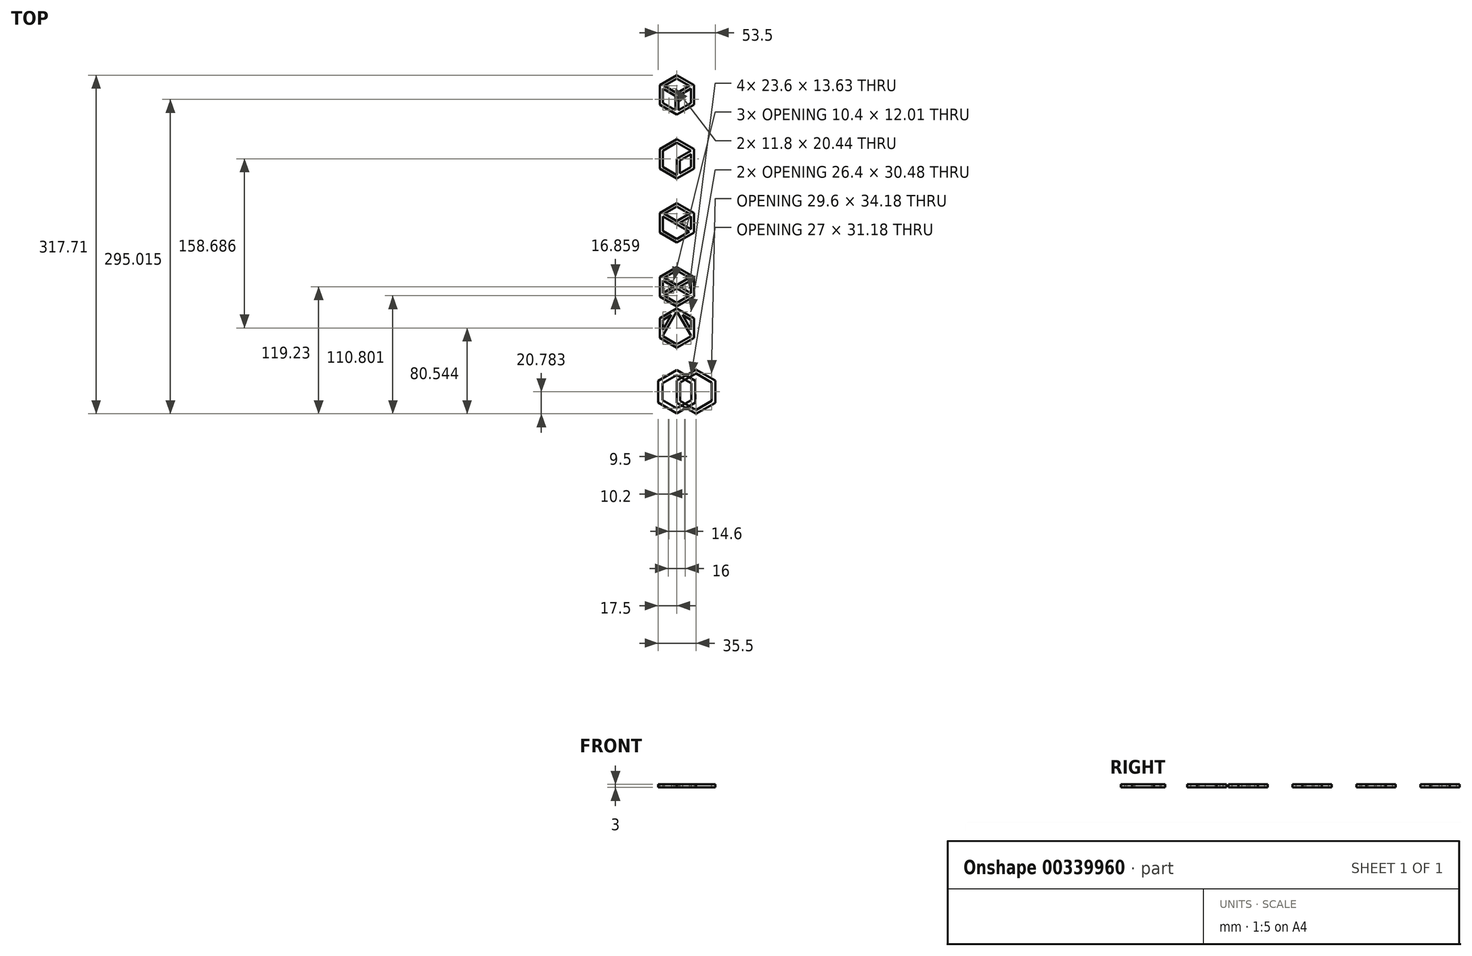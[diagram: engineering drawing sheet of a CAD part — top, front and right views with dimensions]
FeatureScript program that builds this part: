
annotation { "Feature Type Name" : "Feature", "Feature Type Description" : "" }
export const myFeature = defineFeature(function(context is Context, id is Id, definition is map)
    precondition{}
    {
        {
            var Q0;
            Q0=qCreatedBy(makeId("Top.planeOp"),FACE);
            var sketch = newSketch(context, id + "F0", { "sketchPlane" : qUnion([Q0])});
            skCircle(sketch, "E0.cCircle", {"center": v(0, 0) * mm, "radius": 16 * mm, "construction": true});
            skLineSegment(sketch, "E0.0", {"start": v(16, 9.24) * mm, "end": v(16, -9.24) * mm});
            skLineSegment(sketch, "E0.1", {"start": v(16, -9.24) * mm, "end": v(0, -18.48) * mm});
            skLineSegment(sketch, "E0.2", {"start": v(0, -18.48) * mm, "end": v(-16, -9.24) * mm});
            skLineSegment(sketch, "E0.3", {"start": v(-16, -9.24) * mm, "end": v(-16, 9.24) * mm});
            skLineSegment(sketch, "E0.4", {"start": v(-16, 9.24) * mm, "end": v(0, 18.48) * mm});
            skLineSegment(sketch, "E0.5", {"start": v(0, 18.48) * mm, "end": v(16, 9.24) * mm});
            skPoint(sketch, "E0.0.midPoint", {"position": v(16, 0) * mm});
            skLineSegment(sketch, "E1", {"start": v(16, 9.24) * mm, "end": v(0, 0) * mm});
            skLineSegment(sketch, "E2", {"start": v(0, -18.48) * mm, "end": v(0, 0) * mm});
            skLineSegment(sketch, "E3.0", {"start": v(-13.2, 7.62) * mm, "end": v(0, 15.24) * mm});
            skLineSegment(sketch, "E3.1", {"start": v(13.2, 7.62) * mm, "end": v(13.2, -7.62) * mm});
            skLineSegment(sketch, "E3.2", {"start": v(13.2, -7.62) * mm, "end": v(0, -15.24) * mm});
            skLineSegment(sketch, "E3.3", {"start": v(0, 15.24) * mm, "end": v(13.2, 7.62) * mm});
            skLineSegment(sketch, "E3.4", {"start": v(0, -15.24) * mm, "end": v(-13.2, -7.62) * mm});
            skLineSegment(sketch, "E3.5", {"start": v(-13.2, -7.62) * mm, "end": v(-13.2, 7.62) * mm});
            skLineSegment(sketch, "E4.0", {"start": v(2.8, -23.1) * mm, "end": v(2.8, -1.62) * mm});
            skLineSegment(sketch, "E4.1", {"start": v(21.4, 9.12) * mm, "end": v(2.8, -1.62) * mm});
            skSolve(sketch);
        }
        {
            var Q0;
            Q0 = qSketchRegion(id + "F0", true);
            var Q1;
            {var subQ3=sQuery(id+"F0.wireOp",EDGE,"E4.1");var subQ8=sQuery(id+"F0.wireOp",EDGE,"E4.0");var subQ11=makeQuery(id+"F0.imprint","INTERSECT",VERTEX,{"derivedFrom":[subQ8,subQ3]});Q1=makeQuery(id+"F0.imprint","IMPRINT",FACE,{"disambiguationData":[TD([[makeQuery(id+"F0.imprint","IMPRINT",EDGE,{"disambiguationData":[TD([[subQ11,1.0]])],"derivedFrom":subQ8}),1.0]])]});}
            extrude(context, id + "F1", {"entities" : qUnion([Q0, Q1]), "depth" : 3 * mm});
        }
        {
            var Q0;
            Q0=qCreatedBy(makeId("Top.planeOp"),FACE);
            var sketch = newSketch(context, id + "F2", { "sketchPlane" : qUnion([Q0])});
            skCircle(sketch, "E5.cCircle", {"center": v(0, -60) * mm, "radius": 16 * mm, "construction": true});
            skLineSegment(sketch, "E5.0", {"start": v(16, -50.76) * mm, "end": v(16, -69.24) * mm});
            skLineSegment(sketch, "E5.1", {"start": v(16, -69.24) * mm, "end": v(0, -78.48) * mm});
            skLineSegment(sketch, "E5.2", {"start": v(0, -78.48) * mm, "end": v(-16, -69.24) * mm});
            skLineSegment(sketch, "E5.3", {"start": v(-16, -69.24) * mm, "end": v(-16, -50.76) * mm});
            skLineSegment(sketch, "E5.4", {"start": v(-16, -50.76) * mm, "end": v(0, -41.52) * mm});
            skLineSegment(sketch, "E5.5", {"start": v(0, -41.52) * mm, "end": v(16, -50.76) * mm});
            skPoint(sketch, "E5.0.midPoint", {"position": v(16, -60) * mm});
            skLineSegment(sketch, "E6.0", {"start": v(-13.2, -67.62) * mm, "end": v(-13.2, -52.38) * mm});
            skLineSegment(sketch, "E6.1", {"start": v(0, -44.76) * mm, "end": v(13.2, -52.38) * mm});
            skLineSegment(sketch, "E6.2", {"start": v(13.2, -52.38) * mm, "end": v(13.2, -67.62) * mm});
            skLineSegment(sketch, "E6.3", {"start": v(-13.2, -52.38) * mm, "end": v(0, -44.76) * mm});
            skLineSegment(sketch, "E6.4", {"start": v(13.2, -67.62) * mm, "end": v(0, -75.24) * mm});
            skLineSegment(sketch, "E6.5", {"start": v(0, -75.24) * mm, "end": v(-13.2, -67.62) * mm});
            skLineSegment(sketch, "E7", {"start": v(-16, -50.76) * mm, "end": v(16, -69.24) * mm});
            skLineSegment(sketch, "E8", {"start": v(0, -60) * mm, "end": v(16, -50.76) * mm});
            skLineSegment(sketch, "E9.0", {"start": v(-20.7, -49.67) * mm, "end": v(19.3, -72.76) * mm});
            skLineSegment(sketch, "E10.0", {"start": v(-19.3, -47.24) * mm, "end": v(20.7, -70.33) * mm});
            skLineSegment(sketch, "E11.0", {"start": v(-3.3, -63.52) * mm, "end": v(16.7, -51.97) * mm});
            skLineSegment(sketch, "E12.0", {"start": v(-4.7, -61.1) * mm, "end": v(15.3, -49.55) * mm});
            skSolve(sketch);
        }
        {
            var Q0;
            Q0 = qSketchRegion(id + "F2", true);
            var Q1;
            {var subQ4=sQuery(id+"F2.wireOp",EDGE,"E7");var subQ6=sQuery(id+"F2.wireOp",EDGE,"E8");var subQ7=makeQuery(id+"F2.imprint","INTERSECT",VERTEX,{"derivedFrom":[subQ4,subQ6]});Q1=makeQuery(id+"F2.imprint","IMPRINT",FACE,{"disambiguationData":[TD([[makeQuery(id+"F2.imprint","IMPRINT",EDGE,{"disambiguationData":[TD([[subQ7,-1.0]])],"derivedFrom":subQ6}),1.0]])]});}
            var Q2;
            {var subQ0=sQuery(id+"F2.wireOp",EDGE,"E7");var subQ3=makeQuery(id+"F2.imprint","INTERSECT",VERTEX,{"derivedFrom":[subQ0,sQuery(id+"F2.wireOp",EDGE,"E8")]});Q2=makeQuery(id+"F2.imprint","IMPRINT",FACE,{"disambiguationData":[TD([[makeQuery(id+"F2.imprint","IMPRINT",EDGE,{"disambiguationData":[TD([[subQ3,-1.0]])],"derivedFrom":subQ0}),-1.0]])]});}
            var Q3;
            {var subQ1=sQuery(id+"F2.wireOp",EDGE,"E6.2");var subQ3=sQuery(id+"F2.wireOp",EDGE,"E10.0");var subQ4=makeQuery(id+"F2.imprint","INTERSECT",VERTEX,{"derivedFrom":[subQ1,subQ3]});Q3=makeQuery(id+"F2.imprint","IMPRINT",FACE,{"disambiguationData":[TD([[makeQuery(id+"F2.imprint","IMPRINT",EDGE,{"disambiguationData":[TD([[subQ4,1.0]])],"derivedFrom":subQ3}),-1.0]])]});}
            var Q4;
            {var subQ0=sQuery(id+"F2.wireOp",EDGE,"E8");var subQ1=sQuery(id+"F2.wireOp",EDGE,"E7");var subQ2=makeQuery(id+"F2.imprint","INTERSECT",VERTEX,{"derivedFrom":[subQ1,subQ0]});Q4=makeQuery(id+"F2.imprint","IMPRINT",FACE,{"disambiguationData":[TD([[makeQuery(id+"F2.imprint","IMPRINT",EDGE,{"disambiguationData":[TD([[subQ2,-1.0]])],"derivedFrom":subQ1}),1.0]])]});}
            var Q5;
            {var subQ0=sQuery(id+"F2.wireOp",EDGE,"E8");var subQ5=sQuery(id+"F2.wireOp",EDGE,"E10.0");var subQ6=makeQuery(id+"F2.imprint","INTERSECT",VERTEX,{"derivedFrom":[subQ0,subQ5]});Q5=makeQuery(id+"F2.imprint","IMPRINT",FACE,{"disambiguationData":[TD([[makeQuery(id+"F2.imprint","IMPRINT",EDGE,{"disambiguationData":[TD([[subQ6,-1.0]])],"derivedFrom":subQ5}),1.0]])]});}
            var Q6;
            {var subQ3=sQuery(id+"F2.wireOp",EDGE,"E12.0");var subQ5=sQuery(id+"F2.wireOp",EDGE,"E10.0");var subQ7=makeQuery(id+"F2.imprint","INTERSECT",VERTEX,{"derivedFrom":[subQ5,subQ3]});Q6=makeQuery(id+"F2.imprint","IMPRINT",FACE,{"disambiguationData":[TD([[makeQuery(id+"F2.imprint","IMPRINT",EDGE,{"disambiguationData":[TD([[subQ7,-1.0]])],"derivedFrom":subQ5}),1.0]])]});}
            var Q7;
            {var subQ3=sQuery(id+"F2.wireOp",EDGE,"E9.0");var subQ5=sQuery(id+"F2.wireOp",EDGE,"E11.0");var subQ6=makeQuery(id+"F2.imprint","INTERSECT",VERTEX,{"derivedFrom":[subQ3,subQ5]});Q7=makeQuery(id+"F2.imprint","IMPRINT",FACE,{"disambiguationData":[TD([[makeQuery(id+"F2.imprint","IMPRINT",EDGE,{"disambiguationData":[TD([[subQ6,-1.0]])],"derivedFrom":subQ3}),1.0]])]});}
            var Q8;
            {var subQ3=sQuery(id+"F2.wireOp",EDGE,"E9.0");var subQ5=sQuery(id+"F2.wireOp",EDGE,"E12.0");var subQ6=makeQuery(id+"F2.imprint","INTERSECT",VERTEX,{"derivedFrom":[subQ3,subQ5]});Q8=makeQuery(id+"F2.imprint","IMPRINT",FACE,{"disambiguationData":[TD([[makeQuery(id+"F2.imprint","IMPRINT",EDGE,{"disambiguationData":[TD([[subQ6,1.0]])],"derivedFrom":subQ3}),1.0]])]});}
            var Q9;
            {var subQ1=sQuery(id+"F2.wireOp",EDGE,"E6.3");var subQ3=sQuery(id+"F2.wireOp",EDGE,"E10.0");var subQ4=makeQuery(id+"F2.imprint","INTERSECT",VERTEX,{"derivedFrom":[subQ1,subQ3]});Q9=makeQuery(id+"F2.imprint","IMPRINT",FACE,{"disambiguationData":[TD([[makeQuery(id+"F2.imprint","IMPRINT",EDGE,{"disambiguationData":[TD([[subQ4,-1.0]])],"derivedFrom":subQ3}),-1.0]])]});}
            extrude(context, id + "F3", {"entities" : qUnion([Q0, Q1, Q2, Q3, Q4, Q5, Q6, Q7, Q8, Q9]), "depth" : 3 * mm});
        }
        {
            var Q0;
            Q0=qCreatedBy(makeId("Top.planeOp"),FACE);
            var sketch = newSketch(context, id + "F4", { "sketchPlane" : qUnion([Q0])});
            skCircle(sketch, "E13.cCircle", {"center": v(0, 60) * mm, "radius": 16 * mm, "construction": true});
            skLineSegment(sketch, "E13.0", {"start": v(16, 69.24) * mm, "end": v(16, 50.76) * mm});
            skLineSegment(sketch, "E13.1", {"start": v(16, 50.76) * mm, "end": v(0, 41.52) * mm});
            skLineSegment(sketch, "E13.2", {"start": v(0, 41.52) * mm, "end": v(-16, 50.76) * mm});
            skLineSegment(sketch, "E13.3", {"start": v(-16, 50.76) * mm, "end": v(-16, 69.24) * mm});
            skLineSegment(sketch, "E13.4", {"start": v(-16, 69.24) * mm, "end": v(0, 78.48) * mm});
            skLineSegment(sketch, "E13.5", {"start": v(0, 78.48) * mm, "end": v(16, 69.24) * mm});
            skPoint(sketch, "E13.0.midPoint", {"position": v(16, 60) * mm});
            skLineSegment(sketch, "E14.0", {"start": v(-13.2, 67.62) * mm, "end": v(0, 75.24) * mm});
            skLineSegment(sketch, "E14.1", {"start": v(13.2, 67.62) * mm, "end": v(13.2, 52.38) * mm});
            skLineSegment(sketch, "E14.2", {"start": v(13.2, 52.38) * mm, "end": v(0, 44.76) * mm});
            skLineSegment(sketch, "E14.3", {"start": v(0, 75.24) * mm, "end": v(13.2, 67.62) * mm});
            skLineSegment(sketch, "E14.4", {"start": v(0, 44.76) * mm, "end": v(-13.2, 52.38) * mm});
            skLineSegment(sketch, "E14.5", {"start": v(-13.2, 52.38) * mm, "end": v(-13.2, 67.62) * mm});
            skLineSegment(sketch, "E15", {"start": v(0, 41.52) * mm, "end": v(0, 60) * mm});
            skLineSegment(sketch, "E16", {"start": v(0, 60) * mm, "end": v(-16, 69.24) * mm});
            skLineSegment(sketch, "E17", {"start": v(0, 60) * mm, "end": v(16, 69.24) * mm});
            skLineSegment(sketch, "E18.0", {"start": v(0, 61.62) * mm, "end": v(-19.3, 72.76) * mm});
            skLineSegment(sketch, "E18.1", {"start": v(0, 61.62) * mm, "end": v(19.3, 72.76) * mm});
            skLineSegment(sketch, "E19.0", {"start": v(0, 58.38) * mm, "end": v(-20.7, 70.33) * mm});
            skLineSegment(sketch, "E19.1", {"start": v(0, 58.38) * mm, "end": v(20.7, 70.33) * mm});
            skLineSegment(sketch, "E20.0", {"start": v(1.4, 36.9) * mm, "end": v(1.4, 60) * mm});
            skLineSegment(sketch, "E21.0", {"start": v(-1.4, 36.9) * mm, "end": v(-1.4, 60) * mm});
            skSolve(sketch);
        }
        {
            var Q0;
            {var subQ7=sQuery(id+"F4.wireOp",EDGE,"E13.5");var subQ8=sQuery(id+"F4.wireOp",EDGE,"E13.4");var subQ9=makeQuery(id+"F4.imprint","INTERSECT",VERTEX,{"derivedFrom":[subQ8,subQ7]});Q0=makeQuery(id+"F4.imprint","IMPRINT",FACE,{"disambiguationData":[TD([[makeQuery(id+"F4.imprint","IMPRINT",EDGE,{"disambiguationData":[TD([[subQ9,1.0]])],"derivedFrom":subQ8}),-1.0]])]});}
            var Q1;
            {var subQ1=sQuery(id+"F4.wireOp",EDGE,"E13.4");var subQ3=sQuery(id+"F4.wireOp",EDGE,"E18.0");var subQ4=makeQuery(id+"F4.imprint","INTERSECT",VERTEX,{"derivedFrom":[subQ1,subQ3]});Q1=makeQuery(id+"F4.imprint","IMPRINT",FACE,{"disambiguationData":[TD([[makeQuery(id+"F4.imprint","IMPRINT",EDGE,{"disambiguationData":[TD([[subQ4,1.0]])],"derivedFrom":subQ3}),1.0]])]});}
            var Q2;
            {var subQ1=sQuery(id+"F4.wireOp",EDGE,"E13.3");var subQ3=sQuery(id+"F4.wireOp",EDGE,"E19.0");var subQ4=makeQuery(id+"F4.imprint","INTERSECT",VERTEX,{"derivedFrom":[subQ1,subQ3]});Q2=makeQuery(id+"F4.imprint","IMPRINT",FACE,{"disambiguationData":[TD([[makeQuery(id+"F4.imprint","IMPRINT",EDGE,{"disambiguationData":[TD([[subQ4,1.0]])],"derivedFrom":subQ3}),-1.0]])]});}
            var Q3;
            {var subQ0=sQuery(id+"F4.wireOp",EDGE,"E19.0");var subQ3=makeQuery(id+"F4.imprint","INTERSECT",VERTEX,{"derivedFrom":[subQ0,sQuery(id+"F4.wireOp",EDGE,"E21.0")]});Q3=makeQuery(id+"F4.imprint","IMPRINT",FACE,{"disambiguationData":[TD([[makeQuery(id+"F4.imprint","IMPRINT",EDGE,{"disambiguationData":[TD([[subQ3,-1.0]])],"derivedFrom":subQ0}),-1.0]])]});}
            var Q4;
            {var subQ5=sQuery(id+"F4.wireOp",EDGE,"E18.1");var subQ9=sQuery(id+"F4.wireOp",EDGE,"E18.0");var subQ11=makeQuery(id+"F4.imprint","INTERSECT",VERTEX,{"derivedFrom":[subQ9,subQ5]});Q4=makeQuery(id+"F4.imprint","IMPRINT",FACE,{"disambiguationData":[TD([[makeQuery(id+"F4.imprint","IMPRINT",EDGE,{"disambiguationData":[TD([[subQ11,-1.0]])],"derivedFrom":subQ9}),1.0]])]});}
            var Q5;
            {var subQ7=sQuery(id+"F4.wireOp",EDGE,"E13.2");var subQ9=sQuery(id+"F4.wireOp",EDGE,"E13.3");var subQ10=makeQuery(id+"F4.imprint","INTERSECT",VERTEX,{"derivedFrom":[subQ7,subQ9]});Q5=makeQuery(id+"F4.imprint","IMPRINT",FACE,{"disambiguationData":[TD([[makeQuery(id+"F4.imprint","IMPRINT",EDGE,{"disambiguationData":[TD([[subQ10,1.0]])],"derivedFrom":subQ7}),-1.0]])]});}
            var Q6;
            {var subQ3=sQuery(id+"F4.wireOp",EDGE,"E21.0");var subQ5=sQuery(id+"F4.wireOp",EDGE,"E19.0");var subQ7=makeQuery(id+"F4.imprint","INTERSECT",VERTEX,{"derivedFrom":[subQ5,subQ3]});Q6=makeQuery(id+"F4.imprint","IMPRINT",FACE,{"disambiguationData":[TD([[makeQuery(id+"F4.imprint","IMPRINT",EDGE,{"disambiguationData":[TD([[subQ7,1.0]])],"derivedFrom":subQ3}),-1.0]])]});}
            var Q7;
            {var subQ3=sQuery(id+"F4.wireOp",EDGE,"E20.0");var subQ5=sQuery(id+"F4.wireOp",EDGE,"E19.1");var subQ6=makeQuery(id+"F4.imprint","INTERSECT",VERTEX,{"derivedFrom":[subQ5,subQ3]});Q7=makeQuery(id+"F4.imprint","IMPRINT",FACE,{"disambiguationData":[TD([[makeQuery(id+"F4.imprint","IMPRINT",EDGE,{"disambiguationData":[TD([[subQ6,1.0]])],"derivedFrom":subQ3}),1.0]])]});}
            var Q8;
            {var subQ1=sQuery(id+"F4.wireOp",EDGE,"E13.2");var subQ3=sQuery(id+"F4.wireOp",EDGE,"E21.0");var subQ4=makeQuery(id+"F4.imprint","INTERSECT",VERTEX,{"derivedFrom":[subQ1,subQ3]});Q8=makeQuery(id+"F4.imprint","IMPRINT",FACE,{"disambiguationData":[TD([[makeQuery(id+"F4.imprint","IMPRINT",EDGE,{"disambiguationData":[TD([[subQ4,-1.0]])],"derivedFrom":subQ3}),-1.0]])]});}
            var Q9;
            {var subQ1=sQuery(id+"F4.wireOp",EDGE,"E13.1");var subQ3=sQuery(id+"F4.wireOp",EDGE,"E20.0");var subQ4=makeQuery(id+"F4.imprint","INTERSECT",VERTEX,{"derivedFrom":[subQ1,subQ3]});Q9=makeQuery(id+"F4.imprint","IMPRINT",FACE,{"disambiguationData":[TD([[makeQuery(id+"F4.imprint","IMPRINT",EDGE,{"disambiguationData":[TD([[subQ4,-1.0]])],"derivedFrom":subQ3}),1.0]])]});}
            var Q10;
            {var subQ5=sQuery(id+"F4.wireOp",EDGE,"E13.1");var subQ6=sQuery(id+"F4.wireOp",EDGE,"E13.0");var subQ7=makeQuery(id+"F4.imprint","INTERSECT",VERTEX,{"derivedFrom":[subQ6,subQ5]});Q10=makeQuery(id+"F4.imprint","IMPRINT",FACE,{"disambiguationData":[TD([[makeQuery(id+"F4.imprint","IMPRINT",EDGE,{"disambiguationData":[TD([[subQ7,1.0]])],"derivedFrom":subQ6}),-1.0]])]});}
            var Q11;
            {var subQ0=sQuery(id+"F4.wireOp",EDGE,"E19.1");var subQ3=makeQuery(id+"F4.imprint","INTERSECT",VERTEX,{"derivedFrom":[subQ0,sQuery(id+"F4.wireOp",EDGE,"E20.0")]});Q11=makeQuery(id+"F4.imprint","IMPRINT",FACE,{"disambiguationData":[TD([[makeQuery(id+"F4.imprint","IMPRINT",EDGE,{"disambiguationData":[TD([[subQ3,-1.0]])],"derivedFrom":subQ0}),1.0]])]});}
            var Q12;
            {var subQ1=sQuery(id+"F4.wireOp",EDGE,"E13.0");var subQ3=sQuery(id+"F4.wireOp",EDGE,"E19.1");var subQ4=makeQuery(id+"F4.imprint","INTERSECT",VERTEX,{"derivedFrom":[subQ1,subQ3]});Q12=makeQuery(id+"F4.imprint","IMPRINT",FACE,{"disambiguationData":[TD([[makeQuery(id+"F4.imprint","IMPRINT",EDGE,{"disambiguationData":[TD([[subQ4,1.0]])],"derivedFrom":subQ3}),1.0]])]});}
            var Q13;
            {var subQ1=sQuery(id+"F4.wireOp",EDGE,"E13.5");var subQ3=sQuery(id+"F4.wireOp",EDGE,"E18.1");var subQ4=makeQuery(id+"F4.imprint","INTERSECT",VERTEX,{"derivedFrom":[subQ1,subQ3]});Q13=makeQuery(id+"F4.imprint","IMPRINT",FACE,{"disambiguationData":[TD([[makeQuery(id+"F4.imprint","IMPRINT",EDGE,{"disambiguationData":[TD([[subQ4,1.0]])],"derivedFrom":subQ3}),-1.0]])]});}
            extrude(context, id + "F5", {"entities" : qUnion([Q0, Q1, Q2, Q3, Q4, Q5, Q6, Q7, Q8, Q9, Q10, Q11, Q12, Q13]), "depth" : 3 * mm});
        }
        {
            var Q0;
            Q0=qCreatedBy(makeId("Top.planeOp"),FACE);
            var sketch = newSketch(context, id + "F6", { "sketchPlane" : qUnion([Q0])});
            skCircle(sketch, "E22.cCircle", {"center": v(0, -120) * mm, "radius": 16 * mm, "construction": true});
            skLineSegment(sketch, "E22.0", {"start": v(16, -110.76) * mm, "end": v(16, -129.24) * mm});
            skLineSegment(sketch, "E22.1", {"start": v(16, -129.24) * mm, "end": v(0, -138.48) * mm});
            skLineSegment(sketch, "E22.2", {"start": v(0, -138.48) * mm, "end": v(-16, -129.24) * mm});
            skLineSegment(sketch, "E22.3", {"start": v(-16, -129.24) * mm, "end": v(-16, -110.76) * mm});
            skLineSegment(sketch, "E22.4", {"start": v(-16, -110.76) * mm, "end": v(0, -101.52) * mm});
            skLineSegment(sketch, "E22.5", {"start": v(0, -101.52) * mm, "end": v(16, -110.76) * mm});
            skPoint(sketch, "E22.0.midPoint", {"position": v(16, -120) * mm});
            skLineSegment(sketch, "E23", {"start": v(-16, -110.76) * mm, "end": v(16, -129.24) * mm});
            skLineSegment(sketch, "E24", {"start": v(-16, -129.24) * mm, "end": v(16, -110.76) * mm});
            skLineSegment(sketch, "E25.0", {"start": v(-13.2, -127.62) * mm, "end": v(-13.2, -112.38) * mm});
            skLineSegment(sketch, "E25.1", {"start": v(0, -104.76) * mm, "end": v(13.2, -112.38) * mm});
            skLineSegment(sketch, "E25.2", {"start": v(13.2, -112.38) * mm, "end": v(13.2, -127.62) * mm});
            skLineSegment(sketch, "E25.3", {"start": v(-13.2, -112.38) * mm, "end": v(0, -104.76) * mm});
            skLineSegment(sketch, "E25.4", {"start": v(13.2, -127.62) * mm, "end": v(0, -135.24) * mm});
            skLineSegment(sketch, "E25.5", {"start": v(0, -135.24) * mm, "end": v(-13.2, -127.62) * mm});
            skArc(sketch, "E26.0.startCap", {"start": v(-16.7, -111.97) * mm, "mid": v(-17.21, -110.06) * mm, "end": v(-15.3, -109.55) * mm});
            skArc(sketch, "E26.0.endCap", {"start": v(16.7, -128.03) * mm, "mid": v(17.21, -129.94) * mm, "end": v(15.3, -130.45) * mm});
            skLineSegment(sketch, "E26.0.left", {"start": v(-15.3, -109.55) * mm, "end": v(16.7, -128.03) * mm});
            skLineSegment(sketch, "E26.0.right", {"start": v(-16.7, -111.97) * mm, "end": v(15.3, -130.45) * mm});
            skArc(sketch, "E27.0.startCap", {"start": v(-15.3, -130.45) * mm, "mid": v(-17.21, -129.94) * mm, "end": v(-16.7, -128.03) * mm});
            skArc(sketch, "E27.0.endCap", {"start": v(15.3, -109.55) * mm, "mid": v(17.21, -110.06) * mm, "end": v(16.7, -111.97) * mm});
            skLineSegment(sketch, "E27.0.left", {"start": v(-16.7, -128.03) * mm, "end": v(15.3, -109.55) * mm});
            skLineSegment(sketch, "E27.0.right", {"start": v(-15.3, -130.45) * mm, "end": v(16.7, -111.97) * mm});
            skSolve(sketch);
        }
        {
            var Q0;
            {var subQ0=sQuery(id+"F6.wireOp",EDGE,"E27.0.right");var subQ1=sQuery(id+"F6.wireOp",EDGE,"E22.0");var subQ2=makeQuery(id+"F6.imprint","INTERSECT",VERTEX,{"derivedFrom":[subQ1,subQ0]});Q0=makeQuery(id+"F6.imprint","IMPRINT",FACE,{"disambiguationData":[TD([[makeQuery(id+"F6.imprint","IMPRINT",EDGE,{"disambiguationData":[TD([[subQ2,-1.0]])],"derivedFrom":subQ1}),-1.0]])]});}
            var Q1;
            {var subQ5=sQuery(id+"F6.wireOp",EDGE,"E22.2");var subQ6=sQuery(id+"F6.wireOp",EDGE,"E22.1");var subQ7=makeQuery(id+"F6.imprint","INTERSECT",VERTEX,{"derivedFrom":[subQ6,subQ5]});Q1=makeQuery(id+"F6.imprint","IMPRINT",FACE,{"disambiguationData":[TD([[makeQuery(id+"F6.imprint","IMPRINT",EDGE,{"disambiguationData":[TD([[subQ7,1.0]])],"derivedFrom":subQ6}),-1.0]])]});}
            var Q2;
            {var subQ0=sQuery(id+"F6.wireOp",EDGE,"E27.0.left");var subQ1=sQuery(id+"F6.wireOp",EDGE,"E22.3");var subQ2=makeQuery(id+"F6.imprint","INTERSECT",VERTEX,{"derivedFrom":[subQ1,subQ0]});Q2=makeQuery(id+"F6.imprint","IMPRINT",FACE,{"disambiguationData":[TD([[makeQuery(id+"F6.imprint","IMPRINT",EDGE,{"disambiguationData":[TD([[subQ2,-1.0]])],"derivedFrom":subQ1}),-1.0]])]});}
            var Q3;
            {var subQ7=sQuery(id+"F6.wireOp",EDGE,"E22.5");var subQ8=sQuery(id+"F6.wireOp",EDGE,"E22.4");var subQ9=makeQuery(id+"F6.imprint","INTERSECT",VERTEX,{"derivedFrom":[subQ8,subQ7]});Q3=makeQuery(id+"F6.imprint","IMPRINT",FACE,{"disambiguationData":[TD([[makeQuery(id+"F6.imprint","IMPRINT",EDGE,{"disambiguationData":[TD([[subQ9,1.0]])],"derivedFrom":subQ8}),-1.0]])]});}
            var Q4;
            {var subQ1=sQuery(id+"F6.wireOp",EDGE,"E22.0");var subQ3=sQuery(id+"F6.wireOp",EDGE,"E27.0.right");var subQ4=makeQuery(id+"F6.imprint","INTERSECT",VERTEX,{"derivedFrom":[subQ1,subQ3]});Q4=makeQuery(id+"F6.imprint","IMPRINT",FACE,{"disambiguationData":[TD([[makeQuery(id+"F6.imprint","IMPRINT",EDGE,{"disambiguationData":[TD([[subQ4,1.0]])],"derivedFrom":subQ3}),1.0]])]});}
            var Q5;
            {var subQ1=sQuery(id+"F6.wireOp",EDGE,"E22.0");var subQ3=sQuery(id+"F6.wireOp",EDGE,"E26.0.left");var subQ4=makeQuery(id+"F6.imprint","INTERSECT",VERTEX,{"derivedFrom":[subQ1,subQ3]});Q5=makeQuery(id+"F6.imprint","IMPRINT",FACE,{"disambiguationData":[TD([[makeQuery(id+"F6.imprint","IMPRINT",EDGE,{"disambiguationData":[TD([[subQ4,1.0]])],"derivedFrom":subQ3}),-1.0]])]});}
            var Q6;
            {var subQ1=sQuery(id+"F6.wireOp",EDGE,"E22.1");var subQ3=sQuery(id+"F6.wireOp",EDGE,"E26.0.right");var subQ4=makeQuery(id+"F6.imprint","INTERSECT",VERTEX,{"derivedFrom":[subQ1,subQ3]});Q6=makeQuery(id+"F6.imprint","IMPRINT",FACE,{"disambiguationData":[TD([[makeQuery(id+"F6.imprint","IMPRINT",EDGE,{"disambiguationData":[TD([[subQ4,1.0]])],"derivedFrom":subQ3}),1.0]])]});}
            var Q7;
            {var subQ1=sQuery(id+"F6.wireOp",EDGE,"E22.2");var subQ3=sQuery(id+"F6.wireOp",EDGE,"E27.0.right");var subQ4=makeQuery(id+"F6.imprint","INTERSECT",VERTEX,{"derivedFrom":[subQ1,subQ3]});Q7=makeQuery(id+"F6.imprint","IMPRINT",FACE,{"disambiguationData":[TD([[makeQuery(id+"F6.imprint","IMPRINT",EDGE,{"disambiguationData":[TD([[subQ4,-1.0]])],"derivedFrom":subQ3}),1.0]])]});}
            var Q8;
            {var subQ1=sQuery(id+"F6.wireOp",EDGE,"E22.3");var subQ3=sQuery(id+"F6.wireOp",EDGE,"E27.0.left");var subQ4=makeQuery(id+"F6.imprint","INTERSECT",VERTEX,{"derivedFrom":[subQ1,subQ3]});Q8=makeQuery(id+"F6.imprint","IMPRINT",FACE,{"disambiguationData":[TD([[makeQuery(id+"F6.imprint","IMPRINT",EDGE,{"disambiguationData":[TD([[subQ4,-1.0]])],"derivedFrom":subQ3}),-1.0]])]});}
            var Q9;
            {var subQ1=sQuery(id+"F6.wireOp",EDGE,"E22.3");var subQ3=sQuery(id+"F6.wireOp",EDGE,"E26.0.right");var subQ4=makeQuery(id+"F6.imprint","INTERSECT",VERTEX,{"derivedFrom":[subQ1,subQ3]});Q9=makeQuery(id+"F6.imprint","IMPRINT",FACE,{"disambiguationData":[TD([[makeQuery(id+"F6.imprint","IMPRINT",EDGE,{"disambiguationData":[TD([[subQ4,-1.0]])],"derivedFrom":subQ3}),1.0]])]});}
            var Q10;
            {var subQ1=sQuery(id+"F6.wireOp",EDGE,"E22.4");var subQ3=sQuery(id+"F6.wireOp",EDGE,"E26.0.left");var subQ4=makeQuery(id+"F6.imprint","INTERSECT",VERTEX,{"derivedFrom":[subQ1,subQ3]});Q10=makeQuery(id+"F6.imprint","IMPRINT",FACE,{"disambiguationData":[TD([[makeQuery(id+"F6.imprint","IMPRINT",EDGE,{"disambiguationData":[TD([[subQ4,-1.0]])],"derivedFrom":subQ3}),-1.0]])]});}
            var Q11;
            {var subQ1=sQuery(id+"F6.wireOp",EDGE,"E22.5");var subQ3=sQuery(id+"F6.wireOp",EDGE,"E27.0.left");var subQ4=makeQuery(id+"F6.imprint","INTERSECT",VERTEX,{"derivedFrom":[subQ1,subQ3]});Q11=makeQuery(id+"F6.imprint","IMPRINT",FACE,{"disambiguationData":[TD([[makeQuery(id+"F6.imprint","IMPRINT",EDGE,{"disambiguationData":[TD([[subQ4,1.0]])],"derivedFrom":subQ3}),-1.0]])]});}
            var Q12;
            {var subQ1=sQuery(id+"F6.wireOp",EDGE,"E24");var subQ3=sQuery(id+"F6.wireOp",EDGE,"E26.0.right");var subQ4=makeQuery(id+"F6.imprint","INTERSECT",VERTEX,{"derivedFrom":[subQ1,subQ3]});Q12=makeQuery(id+"F6.imprint","IMPRINT",FACE,{"disambiguationData":[TD([[makeQuery(id+"F6.imprint","IMPRINT",EDGE,{"disambiguationData":[TD([[subQ4,1.0]])],"derivedFrom":subQ3}),-1.0]])]});}
            var Q13;
            {var subQ1=sQuery(id+"F6.wireOp",EDGE,"E24");var subQ3=sQuery(id+"F6.wireOp",EDGE,"E26.0.right");var subQ4=makeQuery(id+"F6.imprint","INTERSECT",VERTEX,{"derivedFrom":[subQ1,subQ3]});Q13=makeQuery(id+"F6.imprint","IMPRINT",FACE,{"disambiguationData":[TD([[makeQuery(id+"F6.imprint","IMPRINT",EDGE,{"disambiguationData":[TD([[subQ4,-1.0]])],"derivedFrom":subQ3}),-1.0]])]});}
            var Q14;
            {var subQ0=sQuery(id+"F6.wireOp",EDGE,"E25.0");var subQ5=sQuery(id+"F6.wireOp",EDGE,"E26.0.right");var subQ6=makeQuery(id+"F6.imprint","INTERSECT",VERTEX,{"derivedFrom":[subQ0,subQ5]});Q14=makeQuery(id+"F6.imprint","IMPRINT",FACE,{"disambiguationData":[TD([[makeQuery(id+"F6.imprint","IMPRINT",EDGE,{"disambiguationData":[TD([[subQ6,-1.0]])],"derivedFrom":subQ5}),1.0]])]});}
            var Q15;
            {var subQ0=sQuery(id+"F6.wireOp",EDGE,"E25.3");var subQ5=sQuery(id+"F6.wireOp",EDGE,"E26.0.left");var subQ6=makeQuery(id+"F6.imprint","INTERSECT",VERTEX,{"derivedFrom":[subQ0,subQ5]});Q15=makeQuery(id+"F6.imprint","IMPRINT",FACE,{"disambiguationData":[TD([[makeQuery(id+"F6.imprint","IMPRINT",EDGE,{"disambiguationData":[TD([[subQ6,-1.0]])],"derivedFrom":subQ5}),-1.0]])]});}
            var Q16;
            {var subQ0=sQuery(id+"F6.wireOp",EDGE,"E27.0.left");var subQ1=sQuery(id+"F6.wireOp",EDGE,"E23");var subQ2=makeQuery(id+"F6.imprint","INTERSECT",VERTEX,{"derivedFrom":[subQ1,subQ0]});Q16=makeQuery(id+"F6.imprint","IMPRINT",FACE,{"disambiguationData":[TD([[makeQuery(id+"F6.imprint","IMPRINT",EDGE,{"disambiguationData":[TD([[subQ2,-1.0]])],"derivedFrom":subQ1}),1.0]])]});}
            var Q17;
            {var subQ0=sQuery(id+"F6.wireOp",EDGE,"E27.0.left");var subQ1=sQuery(id+"F6.wireOp",EDGE,"E23");var subQ2=makeQuery(id+"F6.imprint","INTERSECT",VERTEX,{"derivedFrom":[subQ1,subQ0]});Q17=makeQuery(id+"F6.imprint","IMPRINT",FACE,{"disambiguationData":[TD([[makeQuery(id+"F6.imprint","IMPRINT",EDGE,{"disambiguationData":[TD([[subQ2,-1.0]])],"derivedFrom":subQ1}),-1.0]])]});}
            var Q18;
            {var subQ0=sQuery(id+"F6.wireOp",EDGE,"E24");var subQ1=sQuery(id+"F6.wireOp",EDGE,"E23");var subQ2=makeQuery(id+"F6.imprint","INTERSECT",VERTEX,{"derivedFrom":[subQ1,subQ0]});Q18=makeQuery(id+"F6.imprint","IMPRINT",FACE,{"disambiguationData":[TD([[makeQuery(id+"F6.imprint","IMPRINT",EDGE,{"disambiguationData":[TD([[subQ2,-1.0]])],"derivedFrom":subQ1}),-1.0]])]});}
            var Q19;
            {var subQ0=sQuery(id+"F6.wireOp",EDGE,"E24");var subQ1=sQuery(id+"F6.wireOp",EDGE,"E23");var subQ2=makeQuery(id+"F6.imprint","INTERSECT",VERTEX,{"derivedFrom":[subQ1,subQ0]});Q19=makeQuery(id+"F6.imprint","IMPRINT",FACE,{"disambiguationData":[TD([[makeQuery(id+"F6.imprint","IMPRINT",EDGE,{"disambiguationData":[TD([[subQ2,-1.0]])],"derivedFrom":subQ1}),1.0]])]});}
            var Q20;
            {var subQ0=sQuery(id+"F6.wireOp",EDGE,"E25.2");var subQ5=sQuery(id+"F6.wireOp",EDGE,"E26.0.left");var subQ6=makeQuery(id+"F6.imprint","INTERSECT",VERTEX,{"derivedFrom":[subQ0,subQ5]});Q20=makeQuery(id+"F6.imprint","IMPRINT",FACE,{"disambiguationData":[TD([[makeQuery(id+"F6.imprint","IMPRINT",EDGE,{"disambiguationData":[TD([[subQ6,1.0]])],"derivedFrom":subQ5}),-1.0]])]});}
            var Q21;
            {var subQ0=sQuery(id+"F6.wireOp",EDGE,"E25.4");var subQ5=sQuery(id+"F6.wireOp",EDGE,"E26.0.right");var subQ6=makeQuery(id+"F6.imprint","INTERSECT",VERTEX,{"derivedFrom":[subQ0,subQ5]});Q21=makeQuery(id+"F6.imprint","IMPRINT",FACE,{"disambiguationData":[TD([[makeQuery(id+"F6.imprint","IMPRINT",EDGE,{"disambiguationData":[TD([[subQ6,1.0]])],"derivedFrom":subQ5}),1.0]])]});}
            var Q22;
            {var subQ1=sQuery(id+"F6.wireOp",EDGE,"E24");var subQ3=sQuery(id+"F6.wireOp",EDGE,"E26.0.left");var subQ4=makeQuery(id+"F6.imprint","INTERSECT",VERTEX,{"derivedFrom":[subQ1,subQ3]});Q22=makeQuery(id+"F6.imprint","IMPRINT",FACE,{"disambiguationData":[TD([[makeQuery(id+"F6.imprint","IMPRINT",EDGE,{"disambiguationData":[TD([[subQ4,-1.0]])],"derivedFrom":subQ3}),1.0]])]});}
            var Q23;
            {var subQ1=sQuery(id+"F6.wireOp",EDGE,"E24");var subQ3=sQuery(id+"F6.wireOp",EDGE,"E26.0.left");var subQ4=makeQuery(id+"F6.imprint","INTERSECT",VERTEX,{"derivedFrom":[subQ1,subQ3]});Q23=makeQuery(id+"F6.imprint","IMPRINT",FACE,{"disambiguationData":[TD([[makeQuery(id+"F6.imprint","IMPRINT",EDGE,{"disambiguationData":[TD([[subQ4,1.0]])],"derivedFrom":subQ3}),1.0]])]});}
            extrude(context, id + "F7", {"entities" : qUnion([Q0, Q1, Q2, Q3, Q4, Q5, Q6, Q7, Q8, Q9, Q10, Q11, Q12, Q13, Q14, Q15, Q16, Q17, Q18, Q19, Q20, Q21, Q22, Q23]), "depth" : 3 * mm});
        }
        {
            var Q0;
            Q0=qCreatedBy(makeId("Top.planeOp"),FACE);
            var sketch = newSketch(context, id + "F8", { "sketchPlane" : qUnion([Q0])});
            skCircle(sketch, "E28.cCircle", {"center": v(0, -158.69) * mm, "radius": 16 * mm, "construction": true});
            skLineSegment(sketch, "E28.0", {"start": v(16, -149.45) * mm, "end": v(16, -167.92) * mm});
            skLineSegment(sketch, "E28.1", {"start": v(16, -167.92) * mm, "end": v(0, -177.16) * mm});
            skLineSegment(sketch, "E28.2", {"start": v(0, -177.16) * mm, "end": v(-16, -167.92) * mm});
            skLineSegment(sketch, "E28.3", {"start": v(-16, -167.92) * mm, "end": v(-16, -149.45) * mm});
            skLineSegment(sketch, "E28.4", {"start": v(-16, -149.45) * mm, "end": v(0, -140.21) * mm});
            skLineSegment(sketch, "E28.5", {"start": v(0, -140.21) * mm, "end": v(16, -149.45) * mm});
            skPoint(sketch, "E28.0.midPoint", {"position": v(16, -158.69) * mm});
            skLineSegment(sketch, "E29", {"start": v(-16, -167.92) * mm, "end": v(0, -140.21) * mm});
            skLineSegment(sketch, "E30", {"start": v(16, -167.92) * mm, "end": v(0, -140.21) * mm});
            skLineSegment(sketch, "E31.0", {"start": v(-13.2, -166.3) * mm, "end": v(-13.2, -151.07) * mm});
            skLineSegment(sketch, "E31.1", {"start": v(0, -143.44) * mm, "end": v(13.2, -151.07) * mm});
            skLineSegment(sketch, "E31.2", {"start": v(13.2, -151.07) * mm, "end": v(13.2, -166.3) * mm});
            skLineSegment(sketch, "E31.3", {"start": v(-13.2, -151.07) * mm, "end": v(0, -143.44) * mm});
            skLineSegment(sketch, "E31.4", {"start": v(13.2, -166.3) * mm, "end": v(0, -173.93) * mm});
            skLineSegment(sketch, "E31.5", {"start": v(0, -173.93) * mm, "end": v(-13.2, -166.3) * mm});
            skArc(sketch, "E32.0.startCap", {"start": v(-14.79, -168.62) * mm, "mid": v(-16.7, -169.14) * mm, "end": v(-17.21, -167.22) * mm});
            skArc(sketch, "E32.0.endCap", {"start": v(-1.21, -139.51) * mm, "mid": v(0.7, -139) * mm, "end": v(1.21, -140.91) * mm});
            skLineSegment(sketch, "E32.0.left", {"start": v(-17.21, -167.22) * mm, "end": v(-1.21, -139.51) * mm});
            skLineSegment(sketch, "E32.0.right", {"start": v(-14.79, -168.62) * mm, "end": v(1.21, -140.91) * mm});
            skArc(sketch, "E33.0.startCap", {"start": v(17.21, -167.22) * mm, "mid": v(16.7, -169.14) * mm, "end": v(14.79, -168.62) * mm});
            skArc(sketch, "E33.0.endCap", {"start": v(-1.21, -140.91) * mm, "mid": v(-0.7, -139) * mm, "end": v(1.21, -139.51) * mm});
            skLineSegment(sketch, "E33.0.left", {"start": v(14.79, -168.62) * mm, "end": v(-1.21, -140.91) * mm});
            skLineSegment(sketch, "E33.0.right", {"start": v(17.21, -167.22) * mm, "end": v(1.21, -139.51) * mm});
            skSolve(sketch);
        }
        {
            var Q0;
            {var subQ5=sQuery(id+"F8.wireOp",EDGE,"E28.4");var subQ8=sQuery(id+"F8.wireOp",EDGE,"E28.3");var subQ9=makeQuery(id+"F8.imprint","INTERSECT",VERTEX,{"derivedFrom":[subQ8,subQ5]});Q0=makeQuery(id+"F8.imprint","IMPRINT",FACE,{"disambiguationData":[TD([[makeQuery(id+"F8.imprint","IMPRINT",EDGE,{"disambiguationData":[TD([[subQ9,1.0]])],"derivedFrom":subQ8}),-1.0]])]});}
            var Q1;
            {var subQ3=sQuery(id+"F8.wireOp",EDGE,"E31.3");var subQ5=sQuery(id+"F8.wireOp",EDGE,"E29");var subQ6=makeQuery(id+"F8.imprint","INTERSECT",VERTEX,{"derivedFrom":[subQ5,subQ3]});Q1=makeQuery(id+"F8.imprint","IMPRINT",FACE,{"disambiguationData":[TD([[makeQuery(id+"F8.imprint","IMPRINT",EDGE,{"disambiguationData":[TD([[subQ6,-1.0]])],"derivedFrom":subQ5}),1.0]])]});}
            var Q2;
            {var subQ0=sQuery(id+"F8.wireOp",EDGE,"E29");var subQ3=sQuery(id+"F8.wireOp",EDGE,"E33.0.left");var subQ5=makeQuery(id+"F8.imprint","INTERSECT",VERTEX,{"derivedFrom":[subQ0,subQ3]});Q2=makeQuery(id+"F8.imprint","IMPRINT",FACE,{"disambiguationData":[TD([[makeQuery(id+"F8.imprint","IMPRINT",EDGE,{"disambiguationData":[TD([[subQ5,-1.0]])],"derivedFrom":subQ3}),-1.0]])]});}
            var Q3;
            {var subQ0=sQuery(id+"F8.wireOp",EDGE,"E30");var subQ5=sQuery(id+"F8.wireOp",EDGE,"E32.0.right");var subQ6=makeQuery(id+"F8.imprint","INTERSECT",VERTEX,{"derivedFrom":[subQ0,subQ5]});Q3=makeQuery(id+"F8.imprint","IMPRINT",FACE,{"disambiguationData":[TD([[makeQuery(id+"F8.imprint","IMPRINT",EDGE,{"disambiguationData":[TD([[subQ6,1.0]])],"derivedFrom":subQ5}),1.0]])]});}
            var Q4;
            {var subQ0=sQuery(id+"F8.wireOp",EDGE,"E31.3");var subQ1=sQuery(id+"F8.wireOp",EDGE,"E29");var subQ2=makeQuery(id+"F8.imprint","INTERSECT",VERTEX,{"derivedFrom":[subQ1,subQ0]});Q4=makeQuery(id+"F8.imprint","IMPRINT",FACE,{"disambiguationData":[TD([[makeQuery(id+"F8.imprint","IMPRINT",EDGE,{"disambiguationData":[TD([[subQ2,-1.0]])],"derivedFrom":subQ1}),-1.0]])]});}
            var Q5;
            {var subQ0=sQuery(id+"F8.wireOp",EDGE,"E31.3");var subQ1=sQuery(id+"F8.wireOp",EDGE,"E31.1");var subQ2=makeQuery(id+"F8.imprint","INTERSECT",VERTEX,{"derivedFrom":[subQ1,subQ0]});Q5=makeQuery(id+"F8.imprint","IMPRINT",FACE,{"disambiguationData":[TD([[makeQuery(id+"F8.imprint","IMPRINT",EDGE,{"disambiguationData":[TD([[subQ2,-1.0]])],"derivedFrom":subQ1}),1.0]])]});}
            var Q6;
            {var subQ0=sQuery(id+"F8.wireOp",EDGE,"E31.1");var subQ1=sQuery(id+"F8.wireOp",EDGE,"E30");var subQ2=makeQuery(id+"F8.imprint","INTERSECT",VERTEX,{"derivedFrom":[subQ1,subQ0]});Q6=makeQuery(id+"F8.imprint","IMPRINT",FACE,{"disambiguationData":[TD([[makeQuery(id+"F8.imprint","IMPRINT",EDGE,{"disambiguationData":[TD([[subQ2,-1.0]])],"derivedFrom":subQ1}),1.0]])]});}
            var Q7;
            {var subQ3=sQuery(id+"F8.wireOp",EDGE,"E30");var subQ5=sQuery(id+"F8.wireOp",EDGE,"E31.1");var subQ6=makeQuery(id+"F8.imprint","INTERSECT",VERTEX,{"derivedFrom":[subQ3,subQ5]});Q7=makeQuery(id+"F8.imprint","IMPRINT",FACE,{"disambiguationData":[TD([[makeQuery(id+"F8.imprint","IMPRINT",EDGE,{"disambiguationData":[TD([[subQ6,-1.0]])],"derivedFrom":subQ3}),-1.0]])]});}
            var Q8;
            {var subQ0=sQuery(id+"F8.wireOp",EDGE,"E30");var subQ3=sQuery(id+"F8.wireOp",EDGE,"E32.0.right");var subQ5=makeQuery(id+"F8.imprint","INTERSECT",VERTEX,{"derivedFrom":[subQ0,subQ3]});Q8=makeQuery(id+"F8.imprint","IMPRINT",FACE,{"disambiguationData":[TD([[makeQuery(id+"F8.imprint","IMPRINT",EDGE,{"disambiguationData":[TD([[subQ5,-1.0]])],"derivedFrom":subQ3}),1.0]])]});}
            var Q9;
            {var subQ5=sQuery(id+"F8.wireOp",EDGE,"E28.5");var subQ6=sQuery(id+"F8.wireOp",EDGE,"E28.0");var subQ7=makeQuery(id+"F8.imprint","INTERSECT",VERTEX,{"derivedFrom":[subQ6,subQ5]});Q9=makeQuery(id+"F8.imprint","IMPRINT",FACE,{"disambiguationData":[TD([[makeQuery(id+"F8.imprint","IMPRINT",EDGE,{"disambiguationData":[TD([[subQ7,-1.0]])],"derivedFrom":subQ6}),-1.0]])]});}
            var Q10;
            {var subQ0=sQuery(id+"F8.wireOp",EDGE,"E31.2");var subQ1=sQuery(id+"F8.wireOp",EDGE,"E30");var subQ2=makeQuery(id+"F8.imprint","INTERSECT",VERTEX,{"derivedFrom":[subQ1,subQ0]});Q10=makeQuery(id+"F8.imprint","IMPRINT",FACE,{"disambiguationData":[TD([[makeQuery(id+"F8.imprint","IMPRINT",EDGE,{"disambiguationData":[TD([[subQ2,-1.0]])],"derivedFrom":subQ1}),1.0]])]});}
            var Q11;
            {var subQ0=sQuery(id+"F8.wireOp",EDGE,"E31.0");var subQ1=sQuery(id+"F8.wireOp",EDGE,"E29");var subQ2=makeQuery(id+"F8.imprint","INTERSECT",VERTEX,{"derivedFrom":[subQ1,subQ0]});Q11=makeQuery(id+"F8.imprint","IMPRINT",FACE,{"disambiguationData":[TD([[makeQuery(id+"F8.imprint","IMPRINT",EDGE,{"disambiguationData":[TD([[subQ2,-1.0]])],"derivedFrom":subQ1}),-1.0]])]});}
            var Q12;
            {var subQ0=sQuery(id+"F8.wireOp",EDGE,"E31.0");var subQ1=sQuery(id+"F8.wireOp",EDGE,"E29");var subQ2=makeQuery(id+"F8.imprint","INTERSECT",VERTEX,{"derivedFrom":[subQ1,subQ0]});Q12=makeQuery(id+"F8.imprint","IMPRINT",FACE,{"disambiguationData":[TD([[makeQuery(id+"F8.imprint","IMPRINT",EDGE,{"disambiguationData":[TD([[subQ2,-1.0]])],"derivedFrom":subQ1}),1.0]])]});}
            var Q13;
            {var subQ0=sQuery(id+"F8.wireOp",EDGE,"E31.2");var subQ1=sQuery(id+"F8.wireOp",EDGE,"E30");var subQ2=makeQuery(id+"F8.imprint","INTERSECT",VERTEX,{"derivedFrom":[subQ1,subQ0]});Q13=makeQuery(id+"F8.imprint","IMPRINT",FACE,{"disambiguationData":[TD([[makeQuery(id+"F8.imprint","IMPRINT",EDGE,{"disambiguationData":[TD([[subQ2,-1.0]])],"derivedFrom":subQ1}),-1.0]])]});}
            var Q14;
            {var subQ0=sQuery(id+"F8.wireOp",EDGE,"E30");var subQ5=sQuery(id+"F8.wireOp",EDGE,"E31.2");var subQ6=makeQuery(id+"F8.imprint","INTERSECT",VERTEX,{"derivedFrom":[subQ0,subQ5]});Q14=makeQuery(id+"F8.imprint","IMPRINT",FACE,{"disambiguationData":[TD([[makeQuery(id+"F8.imprint","IMPRINT",EDGE,{"disambiguationData":[TD([[subQ6,1.0]])],"derivedFrom":subQ5}),1.0]])]});}
            var Q15;
            {var subQ0=sQuery(id+"F8.wireOp",EDGE,"E30");var subQ5=sQuery(id+"F8.wireOp",EDGE,"E31.2");var subQ6=makeQuery(id+"F8.imprint","INTERSECT",VERTEX,{"derivedFrom":[subQ0,subQ5]});Q15=makeQuery(id+"F8.imprint","IMPRINT",FACE,{"disambiguationData":[TD([[makeQuery(id+"F8.imprint","IMPRINT",EDGE,{"disambiguationData":[TD([[subQ6,-1.0]])],"derivedFrom":subQ5}),1.0]])]});}
            var Q16;
            {var subQ4=sQuery(id+"F8.wireOp",EDGE,"E31.4");Q16=makeQuery(id+"F8.imprint","IMPRINT",FACE,{"disambiguationData":[TD([[makeQuery(id+"F8.imprint","IMPRINT",EDGE,{"derivedFrom":subQ4}),1.0]])]});}
            var Q17;
            {var subQ0=sQuery(id+"F8.wireOp",EDGE,"E29");var subQ5=sQuery(id+"F8.wireOp",EDGE,"E31.0");var subQ6=makeQuery(id+"F8.imprint","INTERSECT",VERTEX,{"derivedFrom":[subQ0,subQ5]});Q17=makeQuery(id+"F8.imprint","IMPRINT",FACE,{"disambiguationData":[TD([[makeQuery(id+"F8.imprint","IMPRINT",EDGE,{"disambiguationData":[TD([[subQ6,1.0]])],"derivedFrom":subQ5}),1.0]])]});}
            var Q18;
            {var subQ0=sQuery(id+"F8.wireOp",EDGE,"E29");var subQ5=sQuery(id+"F8.wireOp",EDGE,"E31.0");var subQ6=makeQuery(id+"F8.imprint","INTERSECT",VERTEX,{"derivedFrom":[subQ0,subQ5]});Q18=makeQuery(id+"F8.imprint","IMPRINT",FACE,{"disambiguationData":[TD([[makeQuery(id+"F8.imprint","IMPRINT",EDGE,{"disambiguationData":[TD([[subQ6,-1.0]])],"derivedFrom":subQ5}),1.0]])]});}
            extrude(context, id + "F9", {"entities" : qUnion([Q0, Q1, Q2, Q3, Q4, Q5, Q6, Q7, Q8, Q9, Q10, Q11, Q12, Q13, Q14, Q15, Q16, Q17, Q18]), "depth" : 3 * mm});
        }
        {
            var Q0;
            Q0=qCreatedBy(makeId("Top.planeOp"),FACE);
            var sketch = newSketch(context, id + "F10", { "sketchPlane" : qUnion([Q0])});
            skCircle(sketch, "E34.cCircle", {"center": v(0, -218.45) * mm, "radius": 17.5 * mm, "construction": true});
            skLineSegment(sketch, "E34.0", {"start": v(17.5, -208.34) * mm, "end": v(17.5, -228.55) * mm});
            skLineSegment(sketch, "E34.1", {"start": v(17.5, -228.55) * mm, "end": v(0, -238.65) * mm});
            skLineSegment(sketch, "E34.2", {"start": v(0, -238.65) * mm, "end": v(-17.5, -228.55) * mm});
            skLineSegment(sketch, "E34.3", {"start": v(-17.5, -228.55) * mm, "end": v(-17.5, -208.34) * mm});
            skLineSegment(sketch, "E34.4", {"start": v(-17.5, -208.34) * mm, "end": v(0, -198.24) * mm});
            skLineSegment(sketch, "E34.5", {"start": v(0, -198.24) * mm, "end": v(17.5, -208.34) * mm});
            skPoint(sketch, "E34.0.midPoint", {"position": v(17.5, -218.45) * mm});
            skLineSegment(sketch, "E35.0", {"start": v(-13.5, -210.65) * mm, "end": v(0, -202.86) * mm});
            skLineSegment(sketch, "E35.1", {"start": v(13.5, -210.65) * mm, "end": v(13.5, -226.24) * mm});
            skLineSegment(sketch, "E35.2", {"start": v(13.5, -226.24) * mm, "end": v(0, -234.04) * mm});
            skLineSegment(sketch, "E35.3", {"start": v(0, -202.86) * mm, "end": v(13.5, -210.65) * mm});
            skLineSegment(sketch, "E35.4", {"start": v(0, -234.04) * mm, "end": v(-13.5, -226.24) * mm});
            skLineSegment(sketch, "E35.5", {"start": v(-13.5, -226.24) * mm, "end": v(-13.5, -210.65) * mm});
            skSolve(sketch);
        }
        {
            var Q0;
            Q0 = qSketchRegion(id + "F10", true);
            extrude(context, id + "F11", {"entities" : qUnion([Q0]), "depth" : 3 * mm});
        }
        {
            var Q0;
            Q0=makeQuery(id+"F11.opExtrude","CAP_FACE",FACE,{"disambiguationData":[OSD([sQuery(id+"F10.wireOp",EDGE,"E34.0"),sQuery(id+"F10.wireOp",EDGE,"E34.1"),sQuery(id+"F10.wireOp",EDGE,"E34.2"),sQuery(id+"F10.wireOp",EDGE,"E34.3"),sQuery(id+"F10.wireOp",EDGE,"E34.4"),sQuery(id+"F10.wireOp",EDGE,"E34.5"),sQuery(id+"F10.wireOp",EDGE,"E35.0"),sQuery(id+"F10.wireOp",EDGE,"E35.1"),sQuery(id+"F10.wireOp",EDGE,"E35.2"),sQuery(id+"F10.wireOp",EDGE,"E35.3"),sQuery(id+"F10.wireOp",EDGE,"E35.4"),sQuery(id+"F10.wireOp",EDGE,"E35.5")])],"isStart":false});
            var sketch = newSketch(context, id + "F12", { "sketchPlane" : qUnion([Q0])});
            skCircle(sketch, "E36.cCircle", {"center": v(18, -218.45) * mm, "radius": 18 * mm, "construction": true});
            skPoint(sketch, "E36.cCircle.centerSnap0", {"position": v(13.5, -218.45) * mm});
            skPoint(sketch, "E36.cCircle.perimeterSnap0", {"position": v(13.5, -218.45) * mm});
            skLineSegment(sketch, "E36.0", {"start": v(0, -228.84) * mm, "end": v(0, -208.05) * mm});
            skLineSegment(sketch, "E36.1", {"start": v(0, -208.05) * mm, "end": v(18, -197.66) * mm});
            skLineSegment(sketch, "E36.2", {"start": v(18, -197.66) * mm, "end": v(36, -208.05) * mm});
            skLineSegment(sketch, "E36.3", {"start": v(36, -208.05) * mm, "end": v(36, -228.84) * mm});
            skLineSegment(sketch, "E36.4", {"start": v(36, -228.84) * mm, "end": v(18, -239.23) * mm});
            skLineSegment(sketch, "E36.5", {"start": v(18, -239.23) * mm, "end": v(0, -228.84) * mm});
            skPoint(sketch, "E36.0.midPoint", {"position": v(0, -218.45) * mm});
            skPoint(sketch, "E36.0.midPoint.positionSnap0", {"position": v(13.5, -218.45) * mm});
            skLineSegment(sketch, "E37.0", {"start": v(3.2, -227) * mm, "end": v(3.2, -209.9) * mm});
            skLineSegment(sketch, "E37.1", {"start": v(18, -201.36) * mm, "end": v(32.8, -209.9) * mm});
            skLineSegment(sketch, "E37.2", {"start": v(32.8, -209.9) * mm, "end": v(32.8, -227) * mm});
            skLineSegment(sketch, "E37.3", {"start": v(3.2, -209.9) * mm, "end": v(18, -201.36) * mm});
            skLineSegment(sketch, "E37.4", {"start": v(32.8, -227) * mm, "end": v(18, -235.54) * mm});
            skLineSegment(sketch, "E37.5", {"start": v(18, -235.54) * mm, "end": v(3.2, -227) * mm});
            skSolve(sketch);
        }
        {
            var Q0;
            Q0 = qSketchRegion(id + "F12", true);
            extrude(context, id + "F13", {"entities" : qUnion([Q0]), "oppositeDirection" : true, "depth" : 3 * mm});
        }
    });
